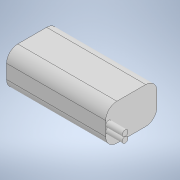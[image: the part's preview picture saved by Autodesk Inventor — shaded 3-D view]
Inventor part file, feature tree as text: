
AUTODESK INVENTOR PART (.ipt)
format: ipt  version: 2022 (Build 260153000, 153)  size: 114,176 bytes
history: native  units: in
note: dims shown in document units (in); Inventor stores cm internally (conversion verified against a paired STEP export)
features: extrude x2, sketch x2, fillet x1
ambient origin geometry x8: Origin, YZ Plane, XZ Plane, XY Plane, X Axis, Y Axis, Z Axis, Center Point
bodies: Solid1 (feature_tree)
feature tree (5):
  extrude  "Extrusion1"  Depth=1.2205in
  extrude  "Extrusion2"  Depth=0.2662in
  fillet  "Fillet1"  Radius=0.3937in
  sketch  "Sketch1"  dims[d0=0.8661in d1=1.2205in]
  sketch  "Sketch2"  dims[d2=2.3622in d3=0.0in d4=0.1378in d6=0.3937in d7=0.0in d8=0.2662in]
